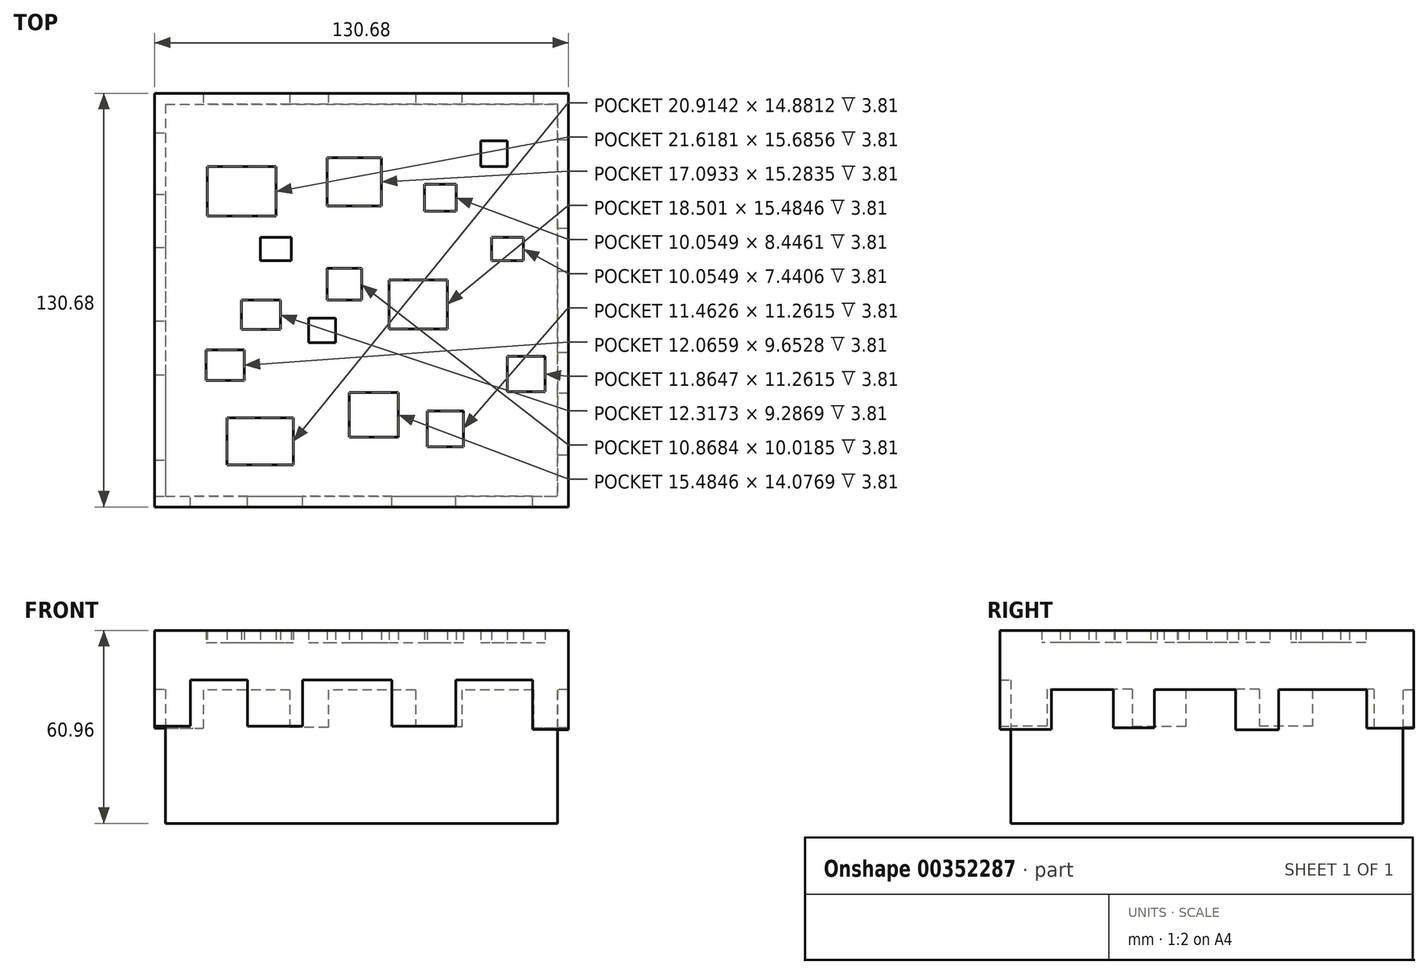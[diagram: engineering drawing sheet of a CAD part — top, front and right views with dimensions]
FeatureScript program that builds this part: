
annotation { "Feature Type Name" : "Feature", "Feature Type Description" : "" }
export const myFeature = defineFeature(function(context is Context, id is Id, definition is map)
    precondition{}
    {
        {
            var Q0;
            Q0=qCreatedBy(makeId("Top.planeOp"),FACE);
            var sketch = newSketch(context, id + "F0", { "sketchPlane" : qUnion([Q0])});
            skLineSegment(sketch, "E0.bottom", {"start": v(-41.27, 41.28) * mm, "end": v(41.28, 41.27) * mm});
            skLineSegment(sketch, "E0.top", {"start": v(-41.27, -41.27) * mm, "end": v(41.28, -41.27) * mm});
            skLineSegment(sketch, "E0.left", {"start": v(-41.27, 41.27) * mm, "end": v(-41.28, -41.27) * mm});
            skLineSegment(sketch, "E0.right", {"start": v(41.28, 41.27) * mm, "end": v(41.28, -41.27) * mm});
            skLineSegment(sketch, "E1", {"start": v(-41.28, 41.28) * mm, "end": v(41.28, -41.28) * mm, "construction": true});
            skLineSegment(sketch, "E2", {"start": v(41.28, 41.28) * mm, "end": v(-41.28, -41.28) * mm, "construction": true});
            skPoint(sketch, "E3", {"position": v(0, 0) * mm});
            skSolve(sketch);
        }
        {
            var Q0;
            Q0 = qSketchRegion(id + "F0", true);
            extrude(context, id + "F1", {"entities" : qUnion([Q0]), "depth" : 38.1 * mm});
        }
        {
            var Q0;
            Q0=makeQuery(id+"F1.opExtrude","CAP_FACE",FACE,{"disambiguationData":[OSD([sQuery(id+"F0.wireOp",EDGE,"E0.bottom"),sQuery(id+"F0.wireOp",EDGE,"E0.top"),sQuery(id+"F0.wireOp",EDGE,"E0.left"),sQuery(id+"F0.wireOp",EDGE,"E0.right")])],"isStart":false});
            var sketch = newSketch(context, id + "F2", { "sketchPlane" : qUnion([Q0])});
            skLineSegment(sketch, "E4.bottom", {"start": v(25.06, 33.5) * mm, "end": v(30.7, 33.5) * mm});
            skLineSegment(sketch, "E4.top", {"start": v(25.06, 28.13) * mm, "end": v(30.7, 28.13) * mm});
            skLineSegment(sketch, "E4.left", {"start": v(25.06, 33.5) * mm, "end": v(25.06, 28.13) * mm});
            skLineSegment(sketch, "E4.right", {"start": v(30.7, 33.5) * mm, "end": v(30.7, 28.13) * mm});
            skLineSegment(sketch, "E5.bottom", {"start": v(-28.3, -34.75) * mm, "end": v(-14.35, -34.75) * mm});
            skLineSegment(sketch, "E5.top", {"start": v(-28.3, -24.83) * mm, "end": v(-14.35, -24.83) * mm});
            skLineSegment(sketch, "E5.left", {"start": v(-28.3, -24.83) * mm, "end": v(-28.3, -34.75) * mm});
            skLineSegment(sketch, "E5.right", {"start": v(-14.35, -24.83) * mm, "end": v(-14.35, -34.75) * mm});
            skLineSegment(sketch, "E6.bottom", {"start": v(-11.13, -3.78) * mm, "end": v(-5.5, -3.78) * mm});
            skLineSegment(sketch, "E6.top", {"start": v(-11.13, -9) * mm, "end": v(-5.5, -9) * mm});
            skLineSegment(sketch, "E6.left", {"start": v(-11.13, -3.78) * mm, "end": v(-11.13, -9) * mm});
            skLineSegment(sketch, "E6.right", {"start": v(-5.5, -3.78) * mm, "end": v(-5.5, -9) * mm});
            skLineSegment(sketch, "E7.bottom", {"start": v(-21.32, 13.25) * mm, "end": v(-14.75, 13.25) * mm});
            skLineSegment(sketch, "E7.top", {"start": v(-21.32, 8.29) * mm, "end": v(-14.75, 8.29) * mm});
            skLineSegment(sketch, "E7.left", {"start": v(-21.32, 13.25) * mm, "end": v(-21.32, 8.29) * mm});
            skLineSegment(sketch, "E7.right", {"start": v(-14.75, 13.25) * mm, "end": v(-14.75, 8.29) * mm});
            skPoint(sketch, "E8.oppositeSnap0", {"position": v(-18.04, 13.25) * mm});
            skLineSegment(sketch, "E8.bottom", {"start": v(-32.45, 28.13) * mm, "end": v(-18.04, 28.13) * mm});
            skLineSegment(sketch, "E8.top", {"start": v(-32.45, 17.67) * mm, "end": v(-18.04, 17.67) * mm});
            skLineSegment(sketch, "E8.left", {"start": v(-32.45, 28.13) * mm, "end": v(-32.45, 17.67) * mm});
            skLineSegment(sketch, "E8.right", {"start": v(-18.04, 28.13) * mm, "end": v(-18.04, 17.67) * mm});
            skLineSegment(sketch, "E9.bottom", {"start": v(-7.25, 30) * mm, "end": v(4.15, 30) * mm});
            skLineSegment(sketch, "E9.top", {"start": v(-7.25, 19.82) * mm, "end": v(4.15, 19.82) * mm});
            skLineSegment(sketch, "E9.left", {"start": v(-7.25, 30) * mm, "end": v(-7.25, 19.82) * mm});
            skLineSegment(sketch, "E9.right", {"start": v(4.15, 30) * mm, "end": v(4.15, 19.82) * mm});
            skLineSegment(sketch, "E10.bottom", {"start": v(5.76, 4.27) * mm, "end": v(18.1, 4.27) * mm});
            skLineSegment(sketch, "E10.top", {"start": v(5.76, -6.06) * mm, "end": v(18.1, -6.06) * mm});
            skLineSegment(sketch, "E10.left", {"start": v(5.76, 4.27) * mm, "end": v(5.76, -6.06) * mm});
            skLineSegment(sketch, "E10.right", {"start": v(18.1, 4.27) * mm, "end": v(18.1, -6.06) * mm});
            skLineSegment(sketch, "E11.bottom", {"start": v(13.27, 24.38) * mm, "end": v(19.97, 24.38) * mm});
            skLineSegment(sketch, "E11.top", {"start": v(13.27, 18.74) * mm, "end": v(19.97, 18.74) * mm});
            skLineSegment(sketch, "E11.left", {"start": v(13.27, 24.38) * mm, "end": v(13.27, 18.74) * mm});
            skLineSegment(sketch, "E11.right", {"start": v(19.97, 24.38) * mm, "end": v(19.97, 18.74) * mm});
            skLineSegment(sketch, "E12.bottom", {"start": v(27.34, 13.25) * mm, "end": v(34.05, 13.25) * mm});
            skLineSegment(sketch, "E12.top", {"start": v(27.34, 8.29) * mm, "end": v(34.05, 8.29) * mm});
            skLineSegment(sketch, "E12.left", {"start": v(27.34, 13.25) * mm, "end": v(27.34, 8.29) * mm});
            skLineSegment(sketch, "E12.right", {"start": v(34.05, 13.25) * mm, "end": v(34.05, 8.29) * mm});
            skLineSegment(sketch, "E13.bottom", {"start": v(13.8, -23.35) * mm, "end": v(21.44, -23.35) * mm});
            skLineSegment(sketch, "E13.top", {"start": v(13.8, -30.86) * mm, "end": v(21.44, -30.86) * mm});
            skLineSegment(sketch, "E13.left", {"start": v(13.8, -23.35) * mm, "end": v(13.8, -30.86) * mm});
            skLineSegment(sketch, "E13.right", {"start": v(21.44, -23.35) * mm, "end": v(21.44, -30.86) * mm});
            skLineSegment(sketch, "E14.bottom", {"start": v(-32.72, -10.48) * mm, "end": v(-24.67, -10.48) * mm});
            skLineSegment(sketch, "E14.top", {"start": v(-32.72, -16.92) * mm, "end": v(-24.67, -16.92) * mm});
            skLineSegment(sketch, "E14.left", {"start": v(-32.72, -10.48) * mm, "end": v(-32.72, -16.92) * mm});
            skLineSegment(sketch, "E14.right", {"start": v(-24.67, -10.48) * mm, "end": v(-24.67, -16.92) * mm});
            skLineSegment(sketch, "E15.bottom", {"start": v(30.7, -11.82) * mm, "end": v(38.6, -11.82) * mm});
            skLineSegment(sketch, "E15.top", {"start": v(30.7, -19.33) * mm, "end": v(38.6, -19.33) * mm});
            skLineSegment(sketch, "E15.left", {"start": v(30.7, -11.82) * mm, "end": v(30.7, -19.33) * mm});
            skLineSegment(sketch, "E15.right", {"start": v(38.6, -11.82) * mm, "end": v(38.6, -19.33) * mm});
            skPoint(sketch, "E16.oppositeSnap0", {"position": v(-25.24, 28.13) * mm});
            skLineSegment(sketch, "E17.bottom", {"start": v(-25.24, 0) * mm, "end": v(-17.03, 0) * mm});
            skLineSegment(sketch, "E17.top", {"start": v(-25.24, -6.2) * mm, "end": v(-17.03, -6.2) * mm});
            skLineSegment(sketch, "E17.left", {"start": v(-25.24, 0) * mm, "end": v(-25.24, -6.2) * mm});
            skLineSegment(sketch, "E17.right", {"start": v(-17.03, 0) * mm, "end": v(-17.03, -6.2) * mm});
            skLineSegment(sketch, "E18.bottom", {"start": v(-7.25, 6.68) * mm, "end": v(0, 6.68) * mm});
            skLineSegment(sketch, "E18.top", {"start": v(-7.25, 0) * mm, "end": v(0, 0) * mm});
            skLineSegment(sketch, "E18.left", {"start": v(-7.25, 6.68) * mm, "end": v(-7.25, 0) * mm});
            skLineSegment(sketch, "E18.right", {"start": v(0, 6.68) * mm, "end": v(0, 0) * mm});
            skLineSegment(sketch, "E19.bottom", {"start": v(-2.55, -19.46) * mm, "end": v(7.77, -19.46) * mm});
            skLineSegment(sketch, "E19.top", {"start": v(-2.55, -28.85) * mm, "end": v(7.77, -28.85) * mm});
            skLineSegment(sketch, "E19.left", {"start": v(-2.55, -19.46) * mm, "end": v(-2.55, -28.85) * mm});
            skLineSegment(sketch, "E19.right", {"start": v(7.77, -19.46) * mm, "end": v(7.77, -28.85) * mm});
            skSolve(sketch);
        }
        {
            var Q0;
            Q0=makeQuery(id+"F2.imprint","IMPRINT",FACE,{"disambiguationData":[TD([[makeQuery(id+"F2.imprint","IMPRINT",EDGE,{"derivedFrom":sQuery(id+"F2.wireOp",EDGE,"E4.bottom")}),1.0]])]});
            extrude(context, id + "F3", {"entities" : qUnion([Q0]), "operationType" : NewBodyOperationType.ADD, "depth" : 2.54 * mm});
        }
        {
            var Q0;
            {var subQ0=sQuery(id+"F0.wireOp",EDGE,"E0.right");Q0=makeQuery(id+"F3.boolean.opBoolean","MERGE",FACE,{"derivedFrom":[makeQuery(id+"F1.opExtrude","SWEPT_FACE",FACE,{"disambiguationData":[OSD([subQ0])]}),makeQuery(id+"F3.opExtrude","SWEPT_FACE",FACE,{"disambiguationData":[OSD([subQ0])]})]});}
            var sketch = newSketch(context, id + "F4", { "sketchPlane" : qUnion([Q0])});
            skLineSegment(sketch, "E20.bottom", {"start": v(-41.27, 40.64) * mm, "end": v(41.27, 40.64) * mm});
            skLineSegment(sketch, "E20.top", {"start": v(-41.27, 28.14) * mm, "end": v(41.27, 28.14) * mm});
            skLineSegment(sketch, "E20.left", {"start": v(-41.27, 40.64) * mm, "end": v(-41.27, 28.14) * mm});
            skLineSegment(sketch, "E20.right", {"start": v(41.27, 40.64) * mm, "end": v(41.27, 28.14) * mm});
            skSolve(sketch);
        }
        {
            var Q0;
            Q0 = qSketchRegion(id + "F4", true);
            extrude(context, id + "F5", {"entities" : qUnion([Q0]), "operationType" : NewBodyOperationType.ADD, "depth" : 2.3 * mm});
        }
        {
            var Q0;
            {var subQ0=sQuery(id+"F0.wireOp",EDGE,"E0.right");Q0=makeQuery(id+"F3.boolean.opBoolean","MERGE",FACE,{"derivedFrom":[makeQuery(id+"F1.opExtrude","SWEPT_FACE",FACE,{"disambiguationData":[OSD([subQ0])]}),makeQuery(id+"F3.opExtrude","SWEPT_FACE",FACE,{"disambiguationData":[OSD([subQ0])]})]});}
            var sketch = newSketch(context, id + "F6", { "sketchPlane" : qUnion([Q0])});
            skLineSegment(sketch, "E21.bottom", {"start": v(-41.27, 19.81) * mm, "end": v(-32.72, 19.81) * mm});
            skLineSegment(sketch, "E21.top", {"start": v(-41.27, 28.14) * mm, "end": v(-32.72, 28.14) * mm});
            skLineSegment(sketch, "E21.left", {"start": v(-41.27, 19.81) * mm, "end": v(-41.27, 28.14) * mm});
            skLineSegment(sketch, "E21.right", {"start": v(-32.72, 19.81) * mm, "end": v(-32.72, 28.14) * mm});
            skSolve(sketch);
        }
        {
            var Q0;
            Q0 = qSketchRegion(id + "F6", true);
            extrude(context, id + "F7", {"entities" : qUnion([Q0]), "operationType" : NewBodyOperationType.ADD, "depth" : 2.3 * mm});
        }
        {
            var Q0;
            {var subQ0=sQuery(id+"F0.wireOp",EDGE,"E0.right");Q0=makeQuery(id+"F3.boolean.opBoolean","MERGE",FACE,{"derivedFrom":[makeQuery(id+"F1.opExtrude","SWEPT_FACE",FACE,{"disambiguationData":[OSD([subQ0])]}),makeQuery(id+"F3.opExtrude","SWEPT_FACE",FACE,{"disambiguationData":[OSD([subQ0])]})]});}
            var sketch = newSketch(context, id + "F8", { "sketchPlane" : qUnion([Q0])});
            skLineSegment(sketch, "E22.bottom", {"start": v(-19.67, 28.14) * mm, "end": v(-11.07, 28.14) * mm});
            skLineSegment(sketch, "E22.top", {"start": v(-19.67, 20.14) * mm, "end": v(-11.07, 20.14) * mm});
            skLineSegment(sketch, "E22.left", {"start": v(-19.67, 28.14) * mm, "end": v(-19.67, 20.14) * mm});
            skLineSegment(sketch, "E22.right", {"start": v(-11.07, 28.14) * mm, "end": v(-11.07, 20.14) * mm});
            skSolve(sketch);
        }
        {
            var Q0;
            Q0 = qSketchRegion(id + "F8", true);
            extrude(context, id + "F9", {"entities" : qUnion([Q0]), "operationType" : NewBodyOperationType.ADD, "depth" : 2.3 * mm});
        }
        {
            var Q0;
            {var subQ0=sQuery(id+"F0.wireOp",EDGE,"E0.right");Q0=makeQuery(id+"F3.boolean.opBoolean","MERGE",FACE,{"derivedFrom":[makeQuery(id+"F1.opExtrude","SWEPT_FACE",FACE,{"disambiguationData":[OSD([subQ0])]}),makeQuery(id+"F3.opExtrude","SWEPT_FACE",FACE,{"disambiguationData":[OSD([subQ0])]})]});}
            var sketch = newSketch(context, id + "F10", { "sketchPlane" : qUnion([Q0])});
            skPoint(sketch, "E23.oppositeSnap0", {"position": v(15.1, 28.14) * mm});
            skLineSegment(sketch, "E23.bottom", {"start": v(6.05, 28.14) * mm, "end": v(15.1, 28.14) * mm});
            skLineSegment(sketch, "E23.top", {"start": v(6.05, 19.66) * mm, "end": v(15.1, 19.66) * mm});
            skLineSegment(sketch, "E23.left", {"start": v(6.05, 28.14) * mm, "end": v(6.05, 19.66) * mm});
            skLineSegment(sketch, "E23.right", {"start": v(15.1, 28.14) * mm, "end": v(15.1, 19.66) * mm});
            skSolve(sketch);
        }
        {
            var Q0;
            Q0 = qSketchRegion(id + "F10", true);
            extrude(context, id + "F11", {"entities" : qUnion([Q0]), "operationType" : NewBodyOperationType.ADD, "depth" : 2.3 * mm});
        }
        {
            var Q0;
            {var subQ0=sQuery(id+"F0.wireOp",EDGE,"E0.right");Q0=makeQuery(id+"F3.boolean.opBoolean","MERGE",FACE,{"derivedFrom":[makeQuery(id+"F1.opExtrude","SWEPT_FACE",FACE,{"disambiguationData":[OSD([subQ0])]}),makeQuery(id+"F3.opExtrude","SWEPT_FACE",FACE,{"disambiguationData":[OSD([subQ0])]})]});}
            var sketch = newSketch(context, id + "F12", { "sketchPlane" : qUnion([Q0])});
            skLineSegment(sketch, "E24.bottom", {"start": v(33.7, 28.14) * mm, "end": v(41.27, 28.14) * mm});
            skLineSegment(sketch, "E24.top", {"start": v(33.7, 20.02) * mm, "end": v(41.27, 20.02) * mm});
            skLineSegment(sketch, "E24.left", {"start": v(33.7, 28.14) * mm, "end": v(33.7, 20.02) * mm});
            skLineSegment(sketch, "E24.right", {"start": v(41.27, 28.14) * mm, "end": v(41.27, 20.02) * mm});
            skLineSegment(sketch, "E25.bottom", {"start": v(33.7, 20.02) * mm, "end": v(30.42, 20.02) * mm});
            skLineSegment(sketch, "E25.top", {"start": v(33.7, 20.02) * mm, "end": v(30.42, 20.02) * mm});
            skLineSegment(sketch, "E25.left", {"start": v(33.7, 20.02) * mm, "end": v(33.7, 20.02) * mm});
            skLineSegment(sketch, "E25.right", {"start": v(30.42, 20.02) * mm, "end": v(30.42, 20.02) * mm});
            skLineSegment(sketch, "E26.top", {"start": v(30.42, 28.14) * mm, "end": v(30.42, 28.14) * mm});
            skLineSegment(sketch, "E26.left", {"start": v(30.42, 20.02) * mm, "end": v(30.42, 28.14) * mm});
            skLineSegment(sketch, "E26.right", {"start": v(30.42, 20.02) * mm, "end": v(30.42, 28.14) * mm});
            skSolve(sketch);
        }
        {
            var Q0;
            Q0 = qSketchRegion(id + "F12", true);
            extrude(context, id + "F13", {"entities" : qUnion([Q0]), "operationType" : NewBodyOperationType.ADD, "depth" : 2.3 * mm});
        }
        {
            var Q0;
            {var subQ0=sQuery(id+"F0.wireOp",EDGE,"E0.bottom");Q0=makeQuery(id+"F13.boolean.opBoolean","MERGE",FACE,{"derivedFrom":[makeQuery(id+"F5.boolean.opBoolean","MERGE",FACE,{"derivedFrom":[makeQuery(id+"F3.boolean.opBoolean","MERGE",FACE,{"derivedFrom":[makeQuery(id+"F1.opExtrude","SWEPT_FACE",FACE,{"disambiguationData":[OSD([subQ0])]}),makeQuery(id+"F3.opExtrude","SWEPT_FACE",FACE,{"disambiguationData":[OSD([subQ0])]})]}),makeQuery(id+"F5.opExtrude","SWEPT_FACE",FACE,{"disambiguationData":[OSD([sQuery(id+"F4.wireOp",EDGE,"E20.right")])]})]}),makeQuery(id+"F13.opExtrude","SWEPT_FACE",FACE,{"disambiguationData":[OSD([sQuery(id+"F12.wireOp",EDGE,"E24.right")])]})]});}
            var sketch = newSketch(context, id + "F14", { "sketchPlane" : qUnion([Q0])});
            skLineSegment(sketch, "E27.bottom", {"start": v(-43.56, 40.64) * mm, "end": v(41.27, 40.64) * mm});
            skLineSegment(sketch, "E27.top", {"start": v(-43.56, 28.04) * mm, "end": v(41.27, 28.04) * mm});
            skLineSegment(sketch, "E27.left", {"start": v(-43.56, 40.64) * mm, "end": v(-43.56, 28.04) * mm});
            skLineSegment(sketch, "E27.right", {"start": v(41.27, 40.64) * mm, "end": v(41.27, 28.04) * mm});
            skSolve(sketch);
        }
        {
            var Q0;
            Q0 = qSketchRegion(id + "F14", true);
            extrude(context, id + "F15", {"entities" : qUnion([Q0]), "operationType" : NewBodyOperationType.ADD, "depth" : 2.3 * mm});
        }
        {
            var Q0;
            {var subQ0=sQuery(id+"F0.wireOp",EDGE,"E0.bottom");Q0=makeQuery(id+"F13.boolean.opBoolean","MERGE",FACE,{"derivedFrom":[makeQuery(id+"F5.boolean.opBoolean","MERGE",FACE,{"derivedFrom":[makeQuery(id+"F3.boolean.opBoolean","MERGE",FACE,{"derivedFrom":[makeQuery(id+"F1.opExtrude","SWEPT_FACE",FACE,{"disambiguationData":[OSD([subQ0])]}),makeQuery(id+"F3.opExtrude","SWEPT_FACE",FACE,{"disambiguationData":[OSD([subQ0])]})]}),makeQuery(id+"F5.opExtrude","SWEPT_FACE",FACE,{"disambiguationData":[OSD([sQuery(id+"F4.wireOp",EDGE,"E20.right")])]})]}),makeQuery(id+"F13.opExtrude","SWEPT_FACE",FACE,{"disambiguationData":[OSD([sQuery(id+"F12.wireOp",EDGE,"E24.right")])]})]});}
            var sketch = newSketch(context, id + "F16", { "sketchPlane" : qUnion([Q0])});
            skLineSegment(sketch, "E28.bottom", {"start": v(-43.56, 20.02) * mm, "end": v(-38.29, 20.02) * mm});
            skLineSegment(sketch, "E28.top", {"start": v(-43.56, 28.04) * mm, "end": v(-38.29, 28.04) * mm});
            skLineSegment(sketch, "E28.left", {"start": v(-43.56, 20.02) * mm, "end": v(-43.56, 28.04) * mm});
            skLineSegment(sketch, "E28.right", {"start": v(-38.29, 20.02) * mm, "end": v(-38.29, 28.04) * mm});
            skSolve(sketch);
        }
        {
            var Q0;
            Q0 = qSketchRegion(id + "F16", true);
            extrude(context, id + "F17", {"entities" : qUnion([Q0]), "operationType" : NewBodyOperationType.ADD, "depth" : 2.3 * mm});
        }
        {
            var Q0;
            {var subQ0=sQuery(id+"F0.wireOp",EDGE,"E0.bottom");Q0=makeQuery(id+"F13.boolean.opBoolean","MERGE",FACE,{"derivedFrom":[makeQuery(id+"F5.boolean.opBoolean","MERGE",FACE,{"derivedFrom":[makeQuery(id+"F3.boolean.opBoolean","MERGE",FACE,{"derivedFrom":[makeQuery(id+"F1.opExtrude","SWEPT_FACE",FACE,{"disambiguationData":[OSD([subQ0])]}),makeQuery(id+"F3.opExtrude","SWEPT_FACE",FACE,{"disambiguationData":[OSD([subQ0])]})]}),makeQuery(id+"F5.opExtrude","SWEPT_FACE",FACE,{"disambiguationData":[OSD([sQuery(id+"F4.wireOp",EDGE,"E20.right")])]})]}),makeQuery(id+"F13.opExtrude","SWEPT_FACE",FACE,{"disambiguationData":[OSD([sQuery(id+"F12.wireOp",EDGE,"E24.right")])]})]});}
            var sketch = newSketch(context, id + "F18", { "sketchPlane" : qUnion([Q0])});
            skLineSegment(sketch, "E29.bottom", {"start": v(-38.29, 28.04) * mm, "end": v(-36.14, 28.04) * mm});
            skLineSegment(sketch, "E29.top", {"start": v(-38.29, 20.02) * mm, "end": v(-36.14, 20.02) * mm});
            skLineSegment(sketch, "E29.left", {"start": v(-38.29, 28.04) * mm, "end": v(-38.29, 20.02) * mm});
            skLineSegment(sketch, "E29.right", {"start": v(-36.14, 28.04) * mm, "end": v(-36.14, 20.02) * mm});
            skSolve(sketch);
        }
        {
            var Q0;
            Q0 = qSketchRegion(id + "F18", true);
            extrude(context, id + "F19", {"entities" : qUnion([Q0]), "operationType" : NewBodyOperationType.ADD, "depth" : 2.3 * mm});
        }
        {
            var Q0;
            {var subQ0=sQuery(id+"F0.wireOp",EDGE,"E0.bottom");Q0=makeQuery(id+"F13.boolean.opBoolean","MERGE",FACE,{"derivedFrom":[makeQuery(id+"F5.boolean.opBoolean","MERGE",FACE,{"derivedFrom":[makeQuery(id+"F3.boolean.opBoolean","MERGE",FACE,{"derivedFrom":[makeQuery(id+"F1.opExtrude","SWEPT_FACE",FACE,{"disambiguationData":[OSD([subQ0])]}),makeQuery(id+"F3.opExtrude","SWEPT_FACE",FACE,{"disambiguationData":[OSD([subQ0])]})]}),makeQuery(id+"F5.opExtrude","SWEPT_FACE",FACE,{"disambiguationData":[OSD([sQuery(id+"F4.wireOp",EDGE,"E20.right")])]})]}),makeQuery(id+"F13.opExtrude","SWEPT_FACE",FACE,{"disambiguationData":[OSD([sQuery(id+"F12.wireOp",EDGE,"E24.right")])]})]});}
            var sketch = newSketch(context, id + "F20", { "sketchPlane" : qUnion([Q0])});
            skLineSegment(sketch, "E30.bottom", {"start": v(-21.16, 28.04) * mm, "end": v(-11.38, 28.04) * mm});
            skLineSegment(sketch, "E30.top", {"start": v(-21.16, 20.27) * mm, "end": v(-11.38, 20.27) * mm});
            skLineSegment(sketch, "E30.left", {"start": v(-21.16, 28.04) * mm, "end": v(-21.16, 20.27) * mm});
            skLineSegment(sketch, "E30.right", {"start": v(-11.38, 28.04) * mm, "end": v(-11.38, 20.27) * mm});
            skSolve(sketch);
        }
        {
            var Q0;
            Q0 = qSketchRegion(id + "F20", true);
            extrude(context, id + "F21", {"entities" : qUnion([Q0]), "operationType" : NewBodyOperationType.ADD, "depth" : 2.3 * mm});
        }
        {
            var Q0;
            {var subQ0=sQuery(id+"F0.wireOp",EDGE,"E0.bottom");Q0=makeQuery(id+"F13.boolean.opBoolean","MERGE",FACE,{"derivedFrom":[makeQuery(id+"F5.boolean.opBoolean","MERGE",FACE,{"derivedFrom":[makeQuery(id+"F3.boolean.opBoolean","MERGE",FACE,{"derivedFrom":[makeQuery(id+"F1.opExtrude","SWEPT_FACE",FACE,{"disambiguationData":[OSD([subQ0])]}),makeQuery(id+"F3.opExtrude","SWEPT_FACE",FACE,{"disambiguationData":[OSD([subQ0])]})]}),makeQuery(id+"F5.opExtrude","SWEPT_FACE",FACE,{"disambiguationData":[OSD([sQuery(id+"F4.wireOp",EDGE,"E20.right")])]})]}),makeQuery(id+"F13.opExtrude","SWEPT_FACE",FACE,{"disambiguationData":[OSD([sQuery(id+"F12.wireOp",EDGE,"E24.right")])]})]});}
            var sketch = newSketch(context, id + "F22", { "sketchPlane" : qUnion([Q0])});
            skLineSegment(sketch, "E31.bottom", {"start": v(7, 28.04) * mm, "end": v(15.08, 28.04) * mm});
            skLineSegment(sketch, "E31.top", {"start": v(7, 20.2) * mm, "end": v(15.08, 20.2) * mm});
            skLineSegment(sketch, "E31.left", {"start": v(7, 28.04) * mm, "end": v(7, 20.2) * mm});
            skLineSegment(sketch, "E31.right", {"start": v(15.08, 28.04) * mm, "end": v(15.08, 20.2) * mm});
            skSolve(sketch);
        }
        {
            var Q0;
            Q0 = qSketchRegion(id + "F22", true);
            extrude(context, id + "F23", {"entities" : qUnion([Q0]), "operationType" : NewBodyOperationType.ADD, "depth" : 2.3 * mm});
        }
        {
            var Q0;
            {var subQ0=sQuery(id+"F0.wireOp",EDGE,"E0.bottom");Q0=makeQuery(id+"F13.boolean.opBoolean","MERGE",FACE,{"derivedFrom":[makeQuery(id+"F5.boolean.opBoolean","MERGE",FACE,{"derivedFrom":[makeQuery(id+"F3.boolean.opBoolean","MERGE",FACE,{"derivedFrom":[makeQuery(id+"F1.opExtrude","SWEPT_FACE",FACE,{"disambiguationData":[OSD([subQ0])]}),makeQuery(id+"F3.opExtrude","SWEPT_FACE",FACE,{"disambiguationData":[OSD([subQ0])]})]}),makeQuery(id+"F5.opExtrude","SWEPT_FACE",FACE,{"disambiguationData":[OSD([sQuery(id+"F4.wireOp",EDGE,"E20.right")])]})]}),makeQuery(id+"F13.opExtrude","SWEPT_FACE",FACE,{"disambiguationData":[OSD([sQuery(id+"F12.wireOp",EDGE,"E24.right")])]})]});}
            var sketch = newSketch(context, id + "F24", { "sketchPlane" : qUnion([Q0])});
            skLineSegment(sketch, "E32.bottom", {"start": v(41.27, 28.04) * mm, "end": v(33.33, 28.04) * mm});
            skLineSegment(sketch, "E32.top", {"start": v(41.27, 20.02) * mm, "end": v(33.33, 20.02) * mm});
            skLineSegment(sketch, "E32.left", {"start": v(41.27, 28.04) * mm, "end": v(41.27, 20.02) * mm});
            skLineSegment(sketch, "E32.right", {"start": v(33.33, 28.04) * mm, "end": v(33.33, 20.02) * mm});
            skSolve(sketch);
        }
        {
            var Q0;
            Q0 = qSketchRegion(id + "F24", true);
            extrude(context, id + "F25", {"entities" : qUnion([Q0]), "operationType" : NewBodyOperationType.ADD, "depth" : 2.3 * mm});
        }
        {
            var Q0;
            {var subQ0=sQuery(id+"F0.wireOp",EDGE,"E0.left");Q0=makeQuery(id+"F25.boolean.opBoolean","MERGE",FACE,{"derivedFrom":[makeQuery(id+"F15.boolean.opBoolean","MERGE",FACE,{"derivedFrom":[makeQuery(id+"F3.boolean.opBoolean","MERGE",FACE,{"derivedFrom":[makeQuery(id+"F1.opExtrude","SWEPT_FACE",FACE,{"disambiguationData":[OSD([subQ0])]}),makeQuery(id+"F3.opExtrude","SWEPT_FACE",FACE,{"disambiguationData":[OSD([subQ0])]})]}),makeQuery(id+"F15.opExtrude","SWEPT_FACE",FACE,{"disambiguationData":[OSD([sQuery(id+"F14.wireOp",EDGE,"E27.right")])]})]}),makeQuery(id+"F25.opExtrude","SWEPT_FACE",FACE,{"disambiguationData":[OSD([sQuery(id+"F24.wireOp",EDGE,"E32.left")])]})]});}
            var sketch = newSketch(context, id + "F26", { "sketchPlane" : qUnion([Q0])});
            skLineSegment(sketch, "E33.bottom", {"start": v(-43.56, 40.64) * mm, "end": v(41.27, 40.64) * mm});
            skLineSegment(sketch, "E33.top", {"start": v(-43.56, 28.22) * mm, "end": v(41.27, 28.22) * mm});
            skLineSegment(sketch, "E33.left", {"start": v(-43.56, 40.64) * mm, "end": v(-43.56, 28.22) * mm});
            skLineSegment(sketch, "E33.right", {"start": v(41.27, 40.64) * mm, "end": v(41.27, 28.22) * mm});
            skSolve(sketch);
        }
        {
            var Q0;
            Q0 = qSketchRegion(id + "F26", true);
            extrude(context, id + "F27", {"entities" : qUnion([Q0]), "operationType" : NewBodyOperationType.ADD, "depth" : 2.3 * mm});
        }
        {
            var Q0;
            {var subQ0=sQuery(id+"F0.wireOp",EDGE,"E0.left");Q0=makeQuery(id+"F25.boolean.opBoolean","MERGE",FACE,{"derivedFrom":[makeQuery(id+"F15.boolean.opBoolean","MERGE",FACE,{"derivedFrom":[makeQuery(id+"F3.boolean.opBoolean","MERGE",FACE,{"derivedFrom":[makeQuery(id+"F1.opExtrude","SWEPT_FACE",FACE,{"disambiguationData":[OSD([subQ0])]}),makeQuery(id+"F3.opExtrude","SWEPT_FACE",FACE,{"disambiguationData":[OSD([subQ0])]})]}),makeQuery(id+"F15.opExtrude","SWEPT_FACE",FACE,{"disambiguationData":[OSD([sQuery(id+"F14.wireOp",EDGE,"E27.right")])]})]}),makeQuery(id+"F25.opExtrude","SWEPT_FACE",FACE,{"disambiguationData":[OSD([sQuery(id+"F24.wireOp",EDGE,"E32.left")])]})]});}
            var sketch = newSketch(context, id + "F28", { "sketchPlane" : qUnion([Q0])});
            skLineSegment(sketch, "E34.bottom", {"start": v(-43.56, 28.22) * mm, "end": v(-37.9, 28.22) * mm});
            skLineSegment(sketch, "E34.top", {"start": v(-43.56, 20.02) * mm, "end": v(-37.9, 20.02) * mm});
            skLineSegment(sketch, "E34.left", {"start": v(-43.56, 28.22) * mm, "end": v(-43.56, 20.02) * mm});
            skLineSegment(sketch, "E34.right", {"start": v(-37.9, 28.22) * mm, "end": v(-37.9, 20.02) * mm});
            skSolve(sketch);
        }
        {
            var Q0;
            Q0 = qSketchRegion(id + "F28", true);
            extrude(context, id + "F29", {"entities" : qUnion([Q0]), "operationType" : NewBodyOperationType.ADD, "depth" : 2.3 * mm});
        }
        {
            var Q0;
            {var subQ0=sQuery(id+"F0.wireOp",EDGE,"E0.left");Q0=makeQuery(id+"F25.boolean.opBoolean","MERGE",FACE,{"derivedFrom":[makeQuery(id+"F15.boolean.opBoolean","MERGE",FACE,{"derivedFrom":[makeQuery(id+"F3.boolean.opBoolean","MERGE",FACE,{"derivedFrom":[makeQuery(id+"F1.opExtrude","SWEPT_FACE",FACE,{"disambiguationData":[OSD([subQ0])]}),makeQuery(id+"F3.opExtrude","SWEPT_FACE",FACE,{"disambiguationData":[OSD([subQ0])]})]}),makeQuery(id+"F15.opExtrude","SWEPT_FACE",FACE,{"disambiguationData":[OSD([sQuery(id+"F14.wireOp",EDGE,"E27.right")])]})]}),makeQuery(id+"F25.opExtrude","SWEPT_FACE",FACE,{"disambiguationData":[OSD([sQuery(id+"F24.wireOp",EDGE,"E32.left")])]})]});}
            var sketch = newSketch(context, id + "F30", { "sketchPlane" : qUnion([Q0])});
            skLineSegment(sketch, "E35.bottom", {"start": v(-37.9, 28.22) * mm, "end": v(-35.2, 28.22) * mm});
            skLineSegment(sketch, "E35.top", {"start": v(-37.9, 20.02) * mm, "end": v(-35.2, 20.02) * mm});
            skLineSegment(sketch, "E35.left", {"start": v(-37.9, 28.22) * mm, "end": v(-37.9, 20.02) * mm});
            skLineSegment(sketch, "E35.right", {"start": v(-35.2, 28.22) * mm, "end": v(-35.2, 20.02) * mm});
            skSolve(sketch);
        }
        {
            var Q0;
            Q0 = qSketchRegion(id + "F30", true);
            extrude(context, id + "F31", {"entities" : qUnion([Q0]), "operationType" : NewBodyOperationType.ADD, "depth" : 2.3 * mm});
        }
        {
            var Q0;
            {var subQ0=sQuery(id+"F0.wireOp",EDGE,"E0.left");Q0=makeQuery(id+"F25.boolean.opBoolean","MERGE",FACE,{"derivedFrom":[makeQuery(id+"F15.boolean.opBoolean","MERGE",FACE,{"derivedFrom":[makeQuery(id+"F3.boolean.opBoolean","MERGE",FACE,{"derivedFrom":[makeQuery(id+"F1.opExtrude","SWEPT_FACE",FACE,{"disambiguationData":[OSD([subQ0])]}),makeQuery(id+"F3.opExtrude","SWEPT_FACE",FACE,{"disambiguationData":[OSD([subQ0])]})]}),makeQuery(id+"F15.opExtrude","SWEPT_FACE",FACE,{"disambiguationData":[OSD([sQuery(id+"F14.wireOp",EDGE,"E27.right")])]})]}),makeQuery(id+"F25.opExtrude","SWEPT_FACE",FACE,{"disambiguationData":[OSD([sQuery(id+"F24.wireOp",EDGE,"E32.left")])]})]});}
            var sketch = newSketch(context, id + "F32", { "sketchPlane" : qUnion([Q0])});
            skLineSegment(sketch, "E36.bottom", {"start": v(-22.25, 28.22) * mm, "end": v(-11.07, 28.22) * mm});
            skLineSegment(sketch, "E36.top", {"start": v(-22.25, 20.48) * mm, "end": v(-11.07, 20.48) * mm});
            skLineSegment(sketch, "E36.left", {"start": v(-22.25, 28.22) * mm, "end": v(-22.25, 20.48) * mm});
            skLineSegment(sketch, "E36.right", {"start": v(-11.07, 28.22) * mm, "end": v(-11.07, 20.48) * mm});
            skSolve(sketch);
        }
        {
            var Q0;
            Q0 = qSketchRegion(id + "F32", true);
            extrude(context, id + "F33", {"entities" : qUnion([Q0]), "operationType" : NewBodyOperationType.ADD, "depth" : 2.3 * mm});
        }
        {
            var Q0;
            {var subQ0=sQuery(id+"F0.wireOp",EDGE,"E0.left");Q0=makeQuery(id+"F25.boolean.opBoolean","MERGE",FACE,{"derivedFrom":[makeQuery(id+"F15.boolean.opBoolean","MERGE",FACE,{"derivedFrom":[makeQuery(id+"F3.boolean.opBoolean","MERGE",FACE,{"derivedFrom":[makeQuery(id+"F1.opExtrude","SWEPT_FACE",FACE,{"disambiguationData":[OSD([subQ0])]}),makeQuery(id+"F3.opExtrude","SWEPT_FACE",FACE,{"disambiguationData":[OSD([subQ0])]})]}),makeQuery(id+"F15.opExtrude","SWEPT_FACE",FACE,{"disambiguationData":[OSD([sQuery(id+"F14.wireOp",EDGE,"E27.right")])]})]}),makeQuery(id+"F25.opExtrude","SWEPT_FACE",FACE,{"disambiguationData":[OSD([sQuery(id+"F24.wireOp",EDGE,"E32.left")])]})]});}
            var sketch = newSketch(context, id + "F34", { "sketchPlane" : qUnion([Q0])});
            skLineSegment(sketch, "E37.bottom", {"start": v(4.4, 28.22) * mm, "end": v(15.7, 28.22) * mm});
            skLineSegment(sketch, "E37.top", {"start": v(4.4, 20.39) * mm, "end": v(15.7, 20.39) * mm});
            skLineSegment(sketch, "E37.left", {"start": v(4.4, 28.22) * mm, "end": v(4.4, 20.39) * mm});
            skLineSegment(sketch, "E37.right", {"start": v(15.7, 28.22) * mm, "end": v(15.7, 20.39) * mm});
            skSolve(sketch);
        }
        {
            var Q0;
            Q0 = qSketchRegion(id + "F34", true);
            extrude(context, id + "F35", {"entities" : qUnion([Q0]), "operationType" : NewBodyOperationType.ADD, "depth" : 2.3 * mm});
        }
        {
            var Q0;
            {var subQ0=sQuery(id+"F0.wireOp",EDGE,"E0.left");Q0=makeQuery(id+"F25.boolean.opBoolean","MERGE",FACE,{"derivedFrom":[makeQuery(id+"F15.boolean.opBoolean","MERGE",FACE,{"derivedFrom":[makeQuery(id+"F3.boolean.opBoolean","MERGE",FACE,{"derivedFrom":[makeQuery(id+"F1.opExtrude","SWEPT_FACE",FACE,{"disambiguationData":[OSD([subQ0])]}),makeQuery(id+"F3.opExtrude","SWEPT_FACE",FACE,{"disambiguationData":[OSD([subQ0])]})]}),makeQuery(id+"F15.opExtrude","SWEPT_FACE",FACE,{"disambiguationData":[OSD([sQuery(id+"F14.wireOp",EDGE,"E27.right")])]})]}),makeQuery(id+"F25.opExtrude","SWEPT_FACE",FACE,{"disambiguationData":[OSD([sQuery(id+"F24.wireOp",EDGE,"E32.left")])]})]});}
            var sketch = newSketch(context, id + "F36", { "sketchPlane" : qUnion([Q0])});
            skLineSegment(sketch, "E38.bottom", {"start": v(33.66, 28.22) * mm, "end": v(41.27, 28.22) * mm});
            skLineSegment(sketch, "E38.top", {"start": v(33.66, 20.48) * mm, "end": v(41.27, 20.48) * mm});
            skLineSegment(sketch, "E38.left", {"start": v(33.66, 28.22) * mm, "end": v(33.66, 20.48) * mm});
            skLineSegment(sketch, "E38.right", {"start": v(41.27, 28.22) * mm, "end": v(41.27, 20.48) * mm});
            skSolve(sketch);
        }
        {
            var Q0;
            Q0 = qSketchRegion(id + "F36", true);
            extrude(context, id + "F37", {"entities" : qUnion([Q0]), "operationType" : NewBodyOperationType.ADD, "depth" : 2.3 * mm});
        }
        {
            var Q0;
            {var subQ0=sQuery(id+"F0.wireOp",EDGE,"E0.top");Q0=makeQuery(id+"F37.boolean.opBoolean","MERGE",FACE,{"derivedFrom":[makeQuery(id+"F27.boolean.opBoolean","MERGE",FACE,{"derivedFrom":[makeQuery(id+"F7.boolean.opBoolean","MERGE",FACE,{"derivedFrom":[makeQuery(id+"F5.boolean.opBoolean","MERGE",FACE,{"derivedFrom":[makeQuery(id+"F3.boolean.opBoolean","MERGE",FACE,{"derivedFrom":[makeQuery(id+"F1.opExtrude","SWEPT_FACE",FACE,{"disambiguationData":[OSD([subQ0])]}),makeQuery(id+"F3.opExtrude","SWEPT_FACE",FACE,{"disambiguationData":[OSD([subQ0])]})]}),makeQuery(id+"F5.opExtrude","SWEPT_FACE",FACE,{"disambiguationData":[OSD([sQuery(id+"F4.wireOp",EDGE,"E20.left")])]})]}),makeQuery(id+"F7.opExtrude","SWEPT_FACE",FACE,{"disambiguationData":[OSD([sQuery(id+"F6.wireOp",EDGE,"E21.left")])]})]}),makeQuery(id+"F27.opExtrude","SWEPT_FACE",FACE,{"disambiguationData":[OSD([sQuery(id+"F26.wireOp",EDGE,"E33.right")])]})]}),makeQuery(id+"F37.opExtrude","SWEPT_FACE",FACE,{"disambiguationData":[OSD([sQuery(id+"F36.wireOp",EDGE,"E38.right")])]})]});}
            var sketch = newSketch(context, id + "F38", { "sketchPlane" : qUnion([Q0])});
            skLineSegment(sketch, "E39.bottom", {"start": v(43.56, 30.23) * mm, "end": v(-43.56, 30.23) * mm});
            skLineSegment(sketch, "E39.top", {"start": v(43.56, 40.64) * mm, "end": v(-43.56, 40.64) * mm});
            skLineSegment(sketch, "E39.left", {"start": v(43.56, 30.23) * mm, "end": v(43.56, 40.64) * mm});
            skLineSegment(sketch, "E39.right", {"start": v(-43.56, 30.23) * mm, "end": v(-43.56, 40.64) * mm});
            skSolve(sketch);
        }
        {
            var Q0;
            Q0 = qSketchRegion(id + "F38", true);
            extrude(context, id + "F39", {"entities" : qUnion([Q0]), "operationType" : NewBodyOperationType.ADD, "depth" : 2.3 * mm});
        }
        {
            var Q0;
            {var subQ0=sQuery(id+"F0.wireOp",EDGE,"E0.top");Q0=makeQuery(id+"F37.boolean.opBoolean","MERGE",FACE,{"derivedFrom":[makeQuery(id+"F27.boolean.opBoolean","MERGE",FACE,{"derivedFrom":[makeQuery(id+"F7.boolean.opBoolean","MERGE",FACE,{"derivedFrom":[makeQuery(id+"F5.boolean.opBoolean","MERGE",FACE,{"derivedFrom":[makeQuery(id+"F3.boolean.opBoolean","MERGE",FACE,{"derivedFrom":[makeQuery(id+"F1.opExtrude","SWEPT_FACE",FACE,{"disambiguationData":[OSD([subQ0])]}),makeQuery(id+"F3.opExtrude","SWEPT_FACE",FACE,{"disambiguationData":[OSD([subQ0])]})]}),makeQuery(id+"F5.opExtrude","SWEPT_FACE",FACE,{"disambiguationData":[OSD([sQuery(id+"F4.wireOp",EDGE,"E20.left")])]})]}),makeQuery(id+"F7.opExtrude","SWEPT_FACE",FACE,{"disambiguationData":[OSD([sQuery(id+"F6.wireOp",EDGE,"E21.left")])]})]}),makeQuery(id+"F27.opExtrude","SWEPT_FACE",FACE,{"disambiguationData":[OSD([sQuery(id+"F26.wireOp",EDGE,"E33.right")])]})]}),makeQuery(id+"F37.opExtrude","SWEPT_FACE",FACE,{"disambiguationData":[OSD([sQuery(id+"F36.wireOp",EDGE,"E38.right")])]})]});}
            var sketch = newSketch(context, id + "F40", { "sketchPlane" : qUnion([Q0])});
            skLineSegment(sketch, "E40.bottom", {"start": v(-43.56, 30.23) * mm, "end": v(-38.63, 30.23) * mm});
            skLineSegment(sketch, "E40.top", {"start": v(-43.56, 20.43) * mm, "end": v(-38.63, 20.43) * mm});
            skLineSegment(sketch, "E40.left", {"start": v(-43.56, 30.23) * mm, "end": v(-43.56, 20.43) * mm});
            skLineSegment(sketch, "E40.right", {"start": v(-38.63, 30.23) * mm, "end": v(-38.63, 20.43) * mm});
            skLineSegment(sketch, "E41.bottom", {"start": v(-38.63, 20.43) * mm, "end": v(-36.06, 20.43) * mm});
            skLineSegment(sketch, "E41.top", {"start": v(-38.63, 30.23) * mm, "end": v(-36.06, 30.23) * mm});
            skLineSegment(sketch, "E41.left", {"start": v(-38.63, 20.43) * mm, "end": v(-38.63, 30.23) * mm});
            skLineSegment(sketch, "E41.right", {"start": v(-36.06, 20.43) * mm, "end": v(-36.06, 30.23) * mm});
            skSolve(sketch);
        }
        {
            var Q0;
            Q0 = qSketchRegion(id + "F40", true);
            extrude(context, id + "F41", {"entities" : qUnion([Q0]), "operationType" : NewBodyOperationType.ADD, "depth" : 2.3 * mm});
        }
        {
            var Q0;
            {var subQ0=sQuery(id+"F0.wireOp",EDGE,"E0.top");Q0=makeQuery(id+"F37.boolean.opBoolean","MERGE",FACE,{"derivedFrom":[makeQuery(id+"F27.boolean.opBoolean","MERGE",FACE,{"derivedFrom":[makeQuery(id+"F7.boolean.opBoolean","MERGE",FACE,{"derivedFrom":[makeQuery(id+"F5.boolean.opBoolean","MERGE",FACE,{"derivedFrom":[makeQuery(id+"F3.boolean.opBoolean","MERGE",FACE,{"derivedFrom":[makeQuery(id+"F1.opExtrude","SWEPT_FACE",FACE,{"disambiguationData":[OSD([subQ0])]}),makeQuery(id+"F3.opExtrude","SWEPT_FACE",FACE,{"disambiguationData":[OSD([subQ0])]})]}),makeQuery(id+"F5.opExtrude","SWEPT_FACE",FACE,{"disambiguationData":[OSD([sQuery(id+"F4.wireOp",EDGE,"E20.left")])]})]}),makeQuery(id+"F7.opExtrude","SWEPT_FACE",FACE,{"disambiguationData":[OSD([sQuery(id+"F6.wireOp",EDGE,"E21.left")])]})]}),makeQuery(id+"F27.opExtrude","SWEPT_FACE",FACE,{"disambiguationData":[OSD([sQuery(id+"F26.wireOp",EDGE,"E33.right")])]})]}),makeQuery(id+"F37.opExtrude","SWEPT_FACE",FACE,{"disambiguationData":[OSD([sQuery(id+"F36.wireOp",EDGE,"E38.right")])]})]});}
            var sketch = newSketch(context, id + "F42", { "sketchPlane" : qUnion([Q0])});
            skLineSegment(sketch, "E42.bottom", {"start": v(-24, 30.23) * mm, "end": v(-12.42, 30.23) * mm});
            skLineSegment(sketch, "E42.top", {"start": v(-24, 20.43) * mm, "end": v(-12.42, 20.43) * mm});
            skLineSegment(sketch, "E42.left", {"start": v(-24, 30.23) * mm, "end": v(-24, 20.43) * mm});
            skLineSegment(sketch, "E42.right", {"start": v(-12.42, 30.23) * mm, "end": v(-12.42, 20.43) * mm});
            skSolve(sketch);
        }
        {
            var Q0;
            Q0 = qSketchRegion(id + "F42", true);
            extrude(context, id + "F43", {"entities" : qUnion([Q0]), "operationType" : NewBodyOperationType.ADD, "depth" : 2.3 * mm});
        }
        {
            var Q0;
            {var subQ0=sQuery(id+"F0.wireOp",EDGE,"E0.top");Q0=makeQuery(id+"F37.boolean.opBoolean","MERGE",FACE,{"derivedFrom":[makeQuery(id+"F27.boolean.opBoolean","MERGE",FACE,{"derivedFrom":[makeQuery(id+"F7.boolean.opBoolean","MERGE",FACE,{"derivedFrom":[makeQuery(id+"F5.boolean.opBoolean","MERGE",FACE,{"derivedFrom":[makeQuery(id+"F3.boolean.opBoolean","MERGE",FACE,{"derivedFrom":[makeQuery(id+"F1.opExtrude","SWEPT_FACE",FACE,{"disambiguationData":[OSD([subQ0])]}),makeQuery(id+"F3.opExtrude","SWEPT_FACE",FACE,{"disambiguationData":[OSD([subQ0])]})]}),makeQuery(id+"F5.opExtrude","SWEPT_FACE",FACE,{"disambiguationData":[OSD([sQuery(id+"F4.wireOp",EDGE,"E20.left")])]})]}),makeQuery(id+"F7.opExtrude","SWEPT_FACE",FACE,{"disambiguationData":[OSD([sQuery(id+"F6.wireOp",EDGE,"E21.left")])]})]}),makeQuery(id+"F27.opExtrude","SWEPT_FACE",FACE,{"disambiguationData":[OSD([sQuery(id+"F26.wireOp",EDGE,"E33.right")])]})]}),makeQuery(id+"F37.opExtrude","SWEPT_FACE",FACE,{"disambiguationData":[OSD([sQuery(id+"F36.wireOp",EDGE,"E38.right")])]})]});}
            var sketch = newSketch(context, id + "F44", { "sketchPlane" : qUnion([Q0])});
            skLineSegment(sketch, "E43.bottom", {"start": v(6.41, 30.23) * mm, "end": v(19.81, 30.23) * mm});
            skLineSegment(sketch, "E43.top", {"start": v(6.41, 20.43) * mm, "end": v(19.81, 20.43) * mm});
            skLineSegment(sketch, "E43.left", {"start": v(6.41, 30.23) * mm, "end": v(6.41, 20.43) * mm});
            skLineSegment(sketch, "E43.right", {"start": v(19.81, 30.23) * mm, "end": v(19.81, 20.43) * mm});
            skSolve(sketch);
        }
        {
            var Q0;
            Q0 = qSketchRegion(id + "F44", true);
            extrude(context, id + "F45", {"entities" : qUnion([Q0]), "operationType" : NewBodyOperationType.ADD, "depth" : 2.3 * mm});
        }
        {
            var Q0;
            {var subQ0=sQuery(id+"F0.wireOp",EDGE,"E0.top");Q0=makeQuery(id+"F37.boolean.opBoolean","MERGE",FACE,{"derivedFrom":[makeQuery(id+"F27.boolean.opBoolean","MERGE",FACE,{"derivedFrom":[makeQuery(id+"F7.boolean.opBoolean","MERGE",FACE,{"derivedFrom":[makeQuery(id+"F5.boolean.opBoolean","MERGE",FACE,{"derivedFrom":[makeQuery(id+"F3.boolean.opBoolean","MERGE",FACE,{"derivedFrom":[makeQuery(id+"F1.opExtrude","SWEPT_FACE",FACE,{"disambiguationData":[OSD([subQ0])]}),makeQuery(id+"F3.opExtrude","SWEPT_FACE",FACE,{"disambiguationData":[OSD([subQ0])]})]}),makeQuery(id+"F5.opExtrude","SWEPT_FACE",FACE,{"disambiguationData":[OSD([sQuery(id+"F4.wireOp",EDGE,"E20.left")])]})]}),makeQuery(id+"F7.opExtrude","SWEPT_FACE",FACE,{"disambiguationData":[OSD([sQuery(id+"F6.wireOp",EDGE,"E21.left")])]})]}),makeQuery(id+"F27.opExtrude","SWEPT_FACE",FACE,{"disambiguationData":[OSD([sQuery(id+"F26.wireOp",EDGE,"E33.right")])]})]}),makeQuery(id+"F37.opExtrude","SWEPT_FACE",FACE,{"disambiguationData":[OSD([sQuery(id+"F36.wireOp",EDGE,"E38.right")])]})]});}
            var sketch = newSketch(context, id + "F46", { "sketchPlane" : qUnion([Q0])});
            skLineSegment(sketch, "E44.bottom", {"start": v(36.04, 30.23) * mm, "end": v(43.56, 30.23) * mm});
            skLineSegment(sketch, "E44.top", {"start": v(36.04, 19.81) * mm, "end": v(43.56, 19.81) * mm});
            skLineSegment(sketch, "E44.left", {"start": v(36.04, 30.23) * mm, "end": v(36.04, 19.81) * mm});
            skLineSegment(sketch, "E44.right", {"start": v(43.56, 30.23) * mm, "end": v(43.56, 19.81) * mm});
            skSolve(sketch);
        }
        {
            var Q0;
            Q0 = qSketchRegion(id + "F46", true);
            extrude(context, id + "F47", {"entities" : qUnion([Q0]), "operationType" : NewBodyOperationType.ADD, "depth" : 2.3 * mm});
        }
        {
            var Q0;
            Q0=makeQuery(id+"F1.opExtrude","SWEPT_BODY",BODY,{"disambiguationData":[OSD([sQuery(id+"F0.wireOp",EDGE,"E0.bottom"),sQuery(id+"F0.wireOp",EDGE,"E0.top"),sQuery(id+"F0.wireOp",EDGE,"E0.left"),sQuery(id+"F0.wireOp",EDGE,"E0.right")])]});
            var Q1;
            Q1=qCreatedBy(makeId("Origin.pointOp"),VERTEX);
            transform(context, id + "F48", {"entities" : qUnion([Q0]), "transformType" : TransformType.SCALE_UNIFORMLY, "scale" : 1.5, "scalePoint" : qUnion([Q1]), "makeCopy" : false});
        }
    });
